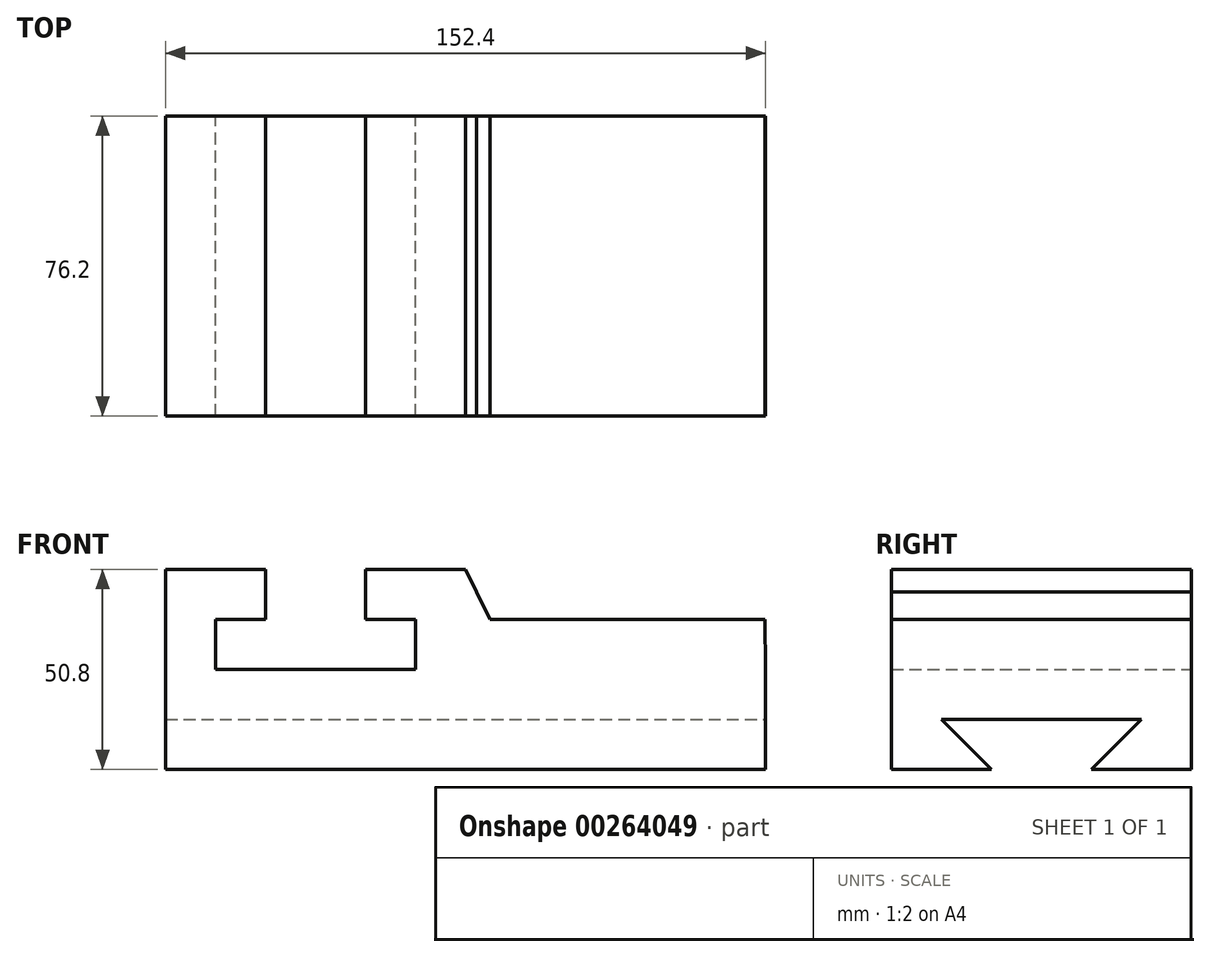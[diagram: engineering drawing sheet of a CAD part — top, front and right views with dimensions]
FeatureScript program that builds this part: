
annotation { "Feature Type Name" : "Feature", "Feature Type Description" : "" }
export const myFeature = defineFeature(function(context is Context, id is Id, definition is map)
    precondition{}
    {
        {
            var Q0;
            Q0=qCreatedBy(makeId("Front.planeOp"),FACE);
            var sketch = newSketch(context, id + "F0", { "sketchPlane" : qUnion([Q0])});
            skLineSegment(sketch, "E0.bottom", {"start": v(-76.2, 0) * mm, "end": v(76.2, 0) * mm});
            skLineSegment(sketch, "E0.left", {"start": v(-76.2, 0) * mm, "end": v(-76.2, 25.4) * mm});
            skLineSegment(sketch, "E0.right", {"start": v(76.2, 0) * mm, "end": v(76.2, 25.4) * mm});
            skLineSegment(sketch, "E1", {"start": v(-76.2, 25.4) * mm, "end": v(-76.2, 50.8) * mm});
            skLineSegment(sketch, "E2", {"start": v(-76.2, 50.8) * mm, "end": v(-50.8, 50.8) * mm});
            skLineSegment(sketch, "E3", {"start": v(-50.8, 50.8) * mm, "end": v(-50.8, 38.1) * mm});
            skLineSegment(sketch, "E4", {"start": v(-50.8, 38.1) * mm, "end": v(-63.5, 38.1) * mm});
            skLineSegment(sketch, "E5", {"start": v(-63.5, 38.1) * mm, "end": v(-63.5, 25.4) * mm});
            skLineSegment(sketch, "E6", {"start": v(-63.5, 25.4) * mm, "end": v(-12.7, 25.4) * mm});
            skLineSegment(sketch, "E7", {"start": v(-12.7, 25.4) * mm, "end": v(-12.7, 38.1) * mm});
            skLineSegment(sketch, "E8", {"start": v(-12.7, 38.1) * mm, "end": v(-25.4, 38.1) * mm});
            skLineSegment(sketch, "E9", {"start": v(-25.4, 38.1) * mm, "end": v(-25.4, 50.8) * mm});
            skLineSegment(sketch, "E10", {"start": v(-25.4, 50.8) * mm, "end": v(0, 50.8) * mm});
            skLineSegment(sketch, "E11", {"start": v(76.1, 38.1) * mm, "end": v(76.2, 25.4) * mm});
            skLineSegment(sketch, "E12", {"start": v(-69.95, 25.4) * mm, "end": v(28.23, 25.4) * mm});
            skLineSegment(sketch, "E13", {"start": v(76.1, 38.1) * mm, "end": v(6.25, 38.1) * mm});
            skLineSegment(sketch, "E14", {"start": v(0, 50.8) * mm, "end": v(2.84, 45.12) * mm});
            skLineSegment(sketch, "E15", {"start": v(6.25, 38.1) * mm, "end": v(2.84, 45.12) * mm});
            skSolve(sketch);
        }
        {
            var Q0;
            Q0=makeQuery(id+"F0.imprint","IMPRINT",FACE,{"disambiguationData":[TD([[makeQuery(id+"F0.imprint","IMPRINT",EDGE,{"derivedFrom":sQuery(id+"F0.wireOp",EDGE,"E0.bottom")}),1.0]])]});
            var Q1;
            Q1 = qSketchRegion(id + "F2", true);
            extrude(context, id + "F1", {"entities" : qUnion([Q0, Q1]), "depth" : 76.2 * mm});
        }
        {
            var Q0;
            Q0=makeQuery(id+"F1.opExtrude","SWEPT_FACE",FACE,{"disambiguationData":[OSD([sQuery(id+"F0.wireOp",EDGE,"E0.right")])]});
            var sketch = newSketch(context, id + "F2", { "sketchPlane" : qUnion([Q0])});
            skLineSegment(sketch, "E16", {"start": v(-76.2, 0) * mm, "end": v(-50.8, 0) * mm});
            skLineSegment(sketch, "E17", {"start": v(0, 0) * mm, "end": v(-25.4, 0) * mm});
            skLineSegment(sketch, "E18", {"start": v(-38.1, 0) * mm, "end": v(-38.1, 12.7) * mm});
            skLineSegment(sketch, "E19", {"start": v(-38.1, 12.7) * mm, "end": v(-12.7, 12.7) * mm});
            skLineSegment(sketch, "E20", {"start": v(-38.1, 12.7) * mm, "end": v(-63.5, 12.7) * mm});
            skLineSegment(sketch, "E21", {"start": v(-25.4, 0) * mm, "end": v(-12.7, 12.7) * mm});
            skLineSegment(sketch, "E22", {"start": v(-50.8, 0) * mm, "end": v(-63.5, 12.7) * mm});
            skSolve(sketch);
        }
        {
            var Q0;
            {var subQ0=sQuery(id+"F2.wireOp",EDGE,"E18");Q0=makeQuery(id+"F2.imprint","IMPRINT",FACE,{"disambiguationData":[TD([[makeQuery(id+"F2.imprint","IMPRINT",EDGE,{"derivedFrom":subQ0}),1.0]])]});}
            var Q1;
            {var subQ0=sQuery(id+"F2.wireOp",EDGE,"E18");Q1=makeQuery(id+"F2.imprint","IMPRINT",FACE,{"disambiguationData":[TD([[makeQuery(id+"F2.imprint","IMPRINT",EDGE,{"derivedFrom":subQ0}),-1.0]])]});}
            extrude(context, id + "F3", {"entities" : qUnion([Q0, Q1]), "operationType" : NewBodyOperationType.REMOVE, "oppositeDirection" : true, "depth" : 152.4 * mm});
        }
    });
